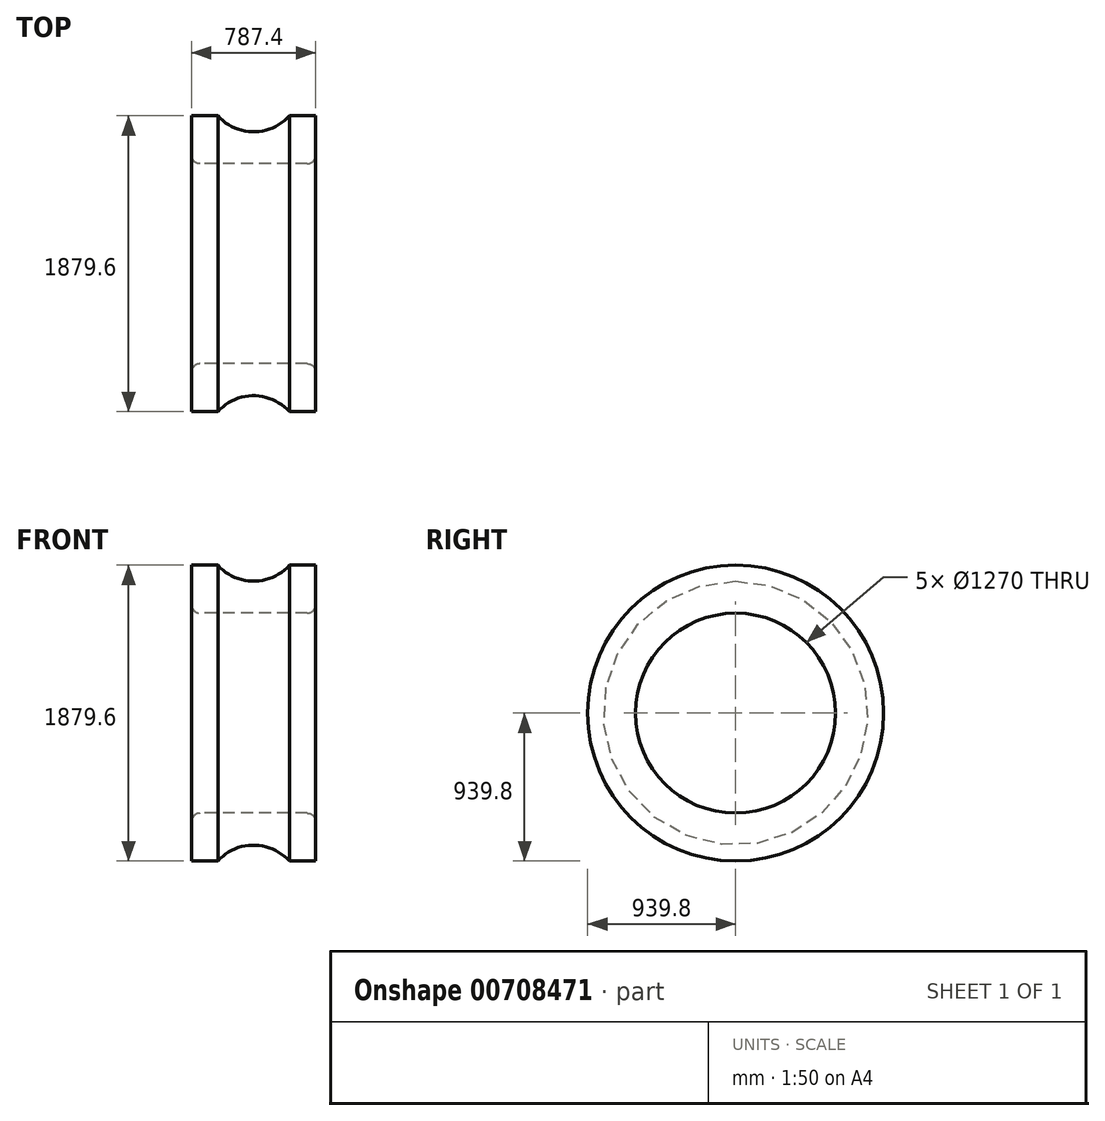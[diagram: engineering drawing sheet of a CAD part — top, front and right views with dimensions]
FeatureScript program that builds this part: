
annotation { "Feature Type Name" : "Feature", "Feature Type Description" : "" }
export const myFeature = defineFeature(function(context is Context, id is Id, definition is map)
    precondition{}
    {
        {
            var Q0;
            Q0=qCreatedBy(makeId("Front.planeOp"),FACE);
            var sketch = newSketch(context, id + "F0", { "sketchPlane" : qUnion([Q0])});
            skLineSegment(sketch, "E0", {"start": v(-572.8, 0) * mm, "end": v(1020.53, 0) * mm});
            skLineSegment(sketch, "E1.bottom", {"start": v(-340.36, 635) * mm, "end": v(340.36, 635) * mm});
            skLineSegment(sketch, "E1.top", {"start": v(-393.7, 939.8) * mm, "end": v(-227.18, 939.8) * mm});
            skLineSegment(sketch, "E1.left", {"start": v(-393.7, 688.34) * mm, "end": v(-393.7, 939.8) * mm});
            skLineSegment(sketch, "E1.right", {"start": v(393.7, 688.34) * mm, "end": v(393.7, 939.8) * mm});
            skPoint(sketch, "E1.middle", {"position": v(0, 787.4) * mm});
            skArc(sketch, "E2", {"start": v(-227.18, 939.8) * mm, "mid": v(0, 838.2) * mm, "end": v(227.18, 939.8) * mm});
            skPoint(sketch, "E2.centerSnap0", {"position": v(0, 939.8) * mm});
            skLineSegment(sketch, "E3", {"start": v(0, 635) * mm, "end": v(0, 0) * mm});
            skLineSegment(sketch, "E4.trimOffspring", {"start": v(227.18, 939.8) * mm, "end": v(393.7, 939.8) * mm});
            skPoint(sketch, "E5.visualSharp", {"position": v(-393.7, 635) * mm});
            skArc(sketch, "E5.filletArc", {"start": v(-393.7, 688.34) * mm, "mid": v(-378.08, 650.62) * mm, "end": v(-340.36, 635) * mm});
            skPoint(sketch, "E6.visualSharp", {"position": v(393.7, 635) * mm});
            skArc(sketch, "E6.filletArc", {"start": v(340.36, 635) * mm, "mid": v(378.08, 650.62) * mm, "end": v(393.7, 688.34) * mm});
            skSolve(sketch);
        }
        {
            var Q0;
            Q0=makeQuery(id+"F0.imprint","IMPRINT",FACE,{"disambiguationData":[TD([[makeQuery(id+"F0.imprint","IMPRINT",EDGE,{"derivedFrom":sQuery(id+"F0.wireOp",EDGE,"E1.top")}),-1.0]])]});
            var Q1;
            Q1=sQuery(id+"F0.wireOp",EDGE,"E0");
            revolve(context, id + "F1", {"surfaceOperationType" : NewSurfaceOperationType.NEW, "entities" : qUnion([Q0]), "axis" : qUnion([Q1]), "revolveType" : RevolveType.FULL});
        }
    });
